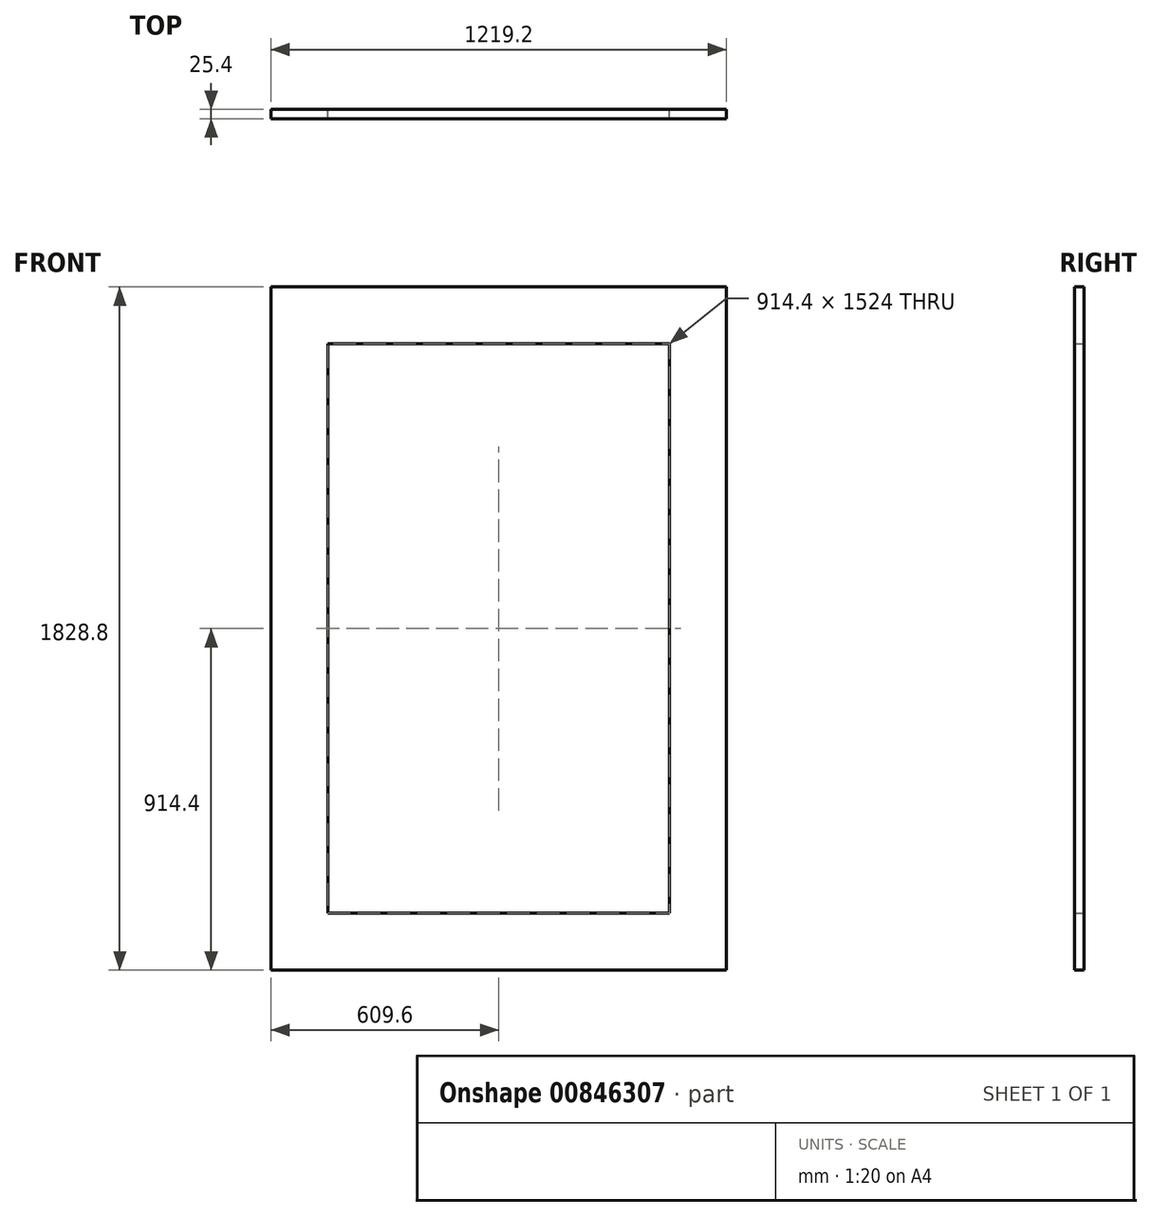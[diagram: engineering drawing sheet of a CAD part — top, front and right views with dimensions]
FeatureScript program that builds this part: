
annotation { "Feature Type Name" : "Feature", "Feature Type Description" : "" }
export const myFeature = defineFeature(function(context is Context, id is Id, definition is map)
    precondition{}
    {
        {
            var Q0;
            Q0=qCreatedBy(makeId("Front.planeOp"),FACE);
            var sketch = newSketch(context, id + "F0", { "sketchPlane" : qUnion([Q0])});
            skLineSegment(sketch, "E0.bottom", {"start": v(-609.6, 914.4) * mm, "end": v(609.6, 914.4) * mm});
            skLineSegment(sketch, "E0.top", {"start": v(-609.6, -914.4) * mm, "end": v(609.6, -914.4) * mm});
            skLineSegment(sketch, "E0.left", {"start": v(-609.6, 914.4) * mm, "end": v(-609.6, -914.4) * mm});
            skLineSegment(sketch, "E0.right", {"start": v(609.6, 914.4) * mm, "end": v(609.6, -914.4) * mm});
            skLineSegment(sketch, "E1.0", {"start": v(457.2, 762) * mm, "end": v(457.2, -762) * mm});
            skLineSegment(sketch, "E1.1", {"start": v(-457.2, 762) * mm, "end": v(457.2, 762) * mm});
            skLineSegment(sketch, "E1.2", {"start": v(-457.2, 762) * mm, "end": v(-457.2, -762) * mm});
            skLineSegment(sketch, "E1.3", {"start": v(-457.2, -762) * mm, "end": v(457.2, -762) * mm});
            skSolve(sketch);
        }
        {
            var Q0;
            Q0=makeQuery(id+"F0.imprint","IMPRINT",FACE,{"disambiguationData":[TD([[makeQuery(id+"F0.imprint","IMPRINT",EDGE,{"derivedFrom":sQuery(id+"F0.wireOp",EDGE,"E0.bottom")}),-1.0]])]});
            extrude(context, id + "F1", {"entities" : qUnion([Q0]), "depth" : 25.4 * mm, "offsetDistance" : 25.4 * mm});
        }
    });
